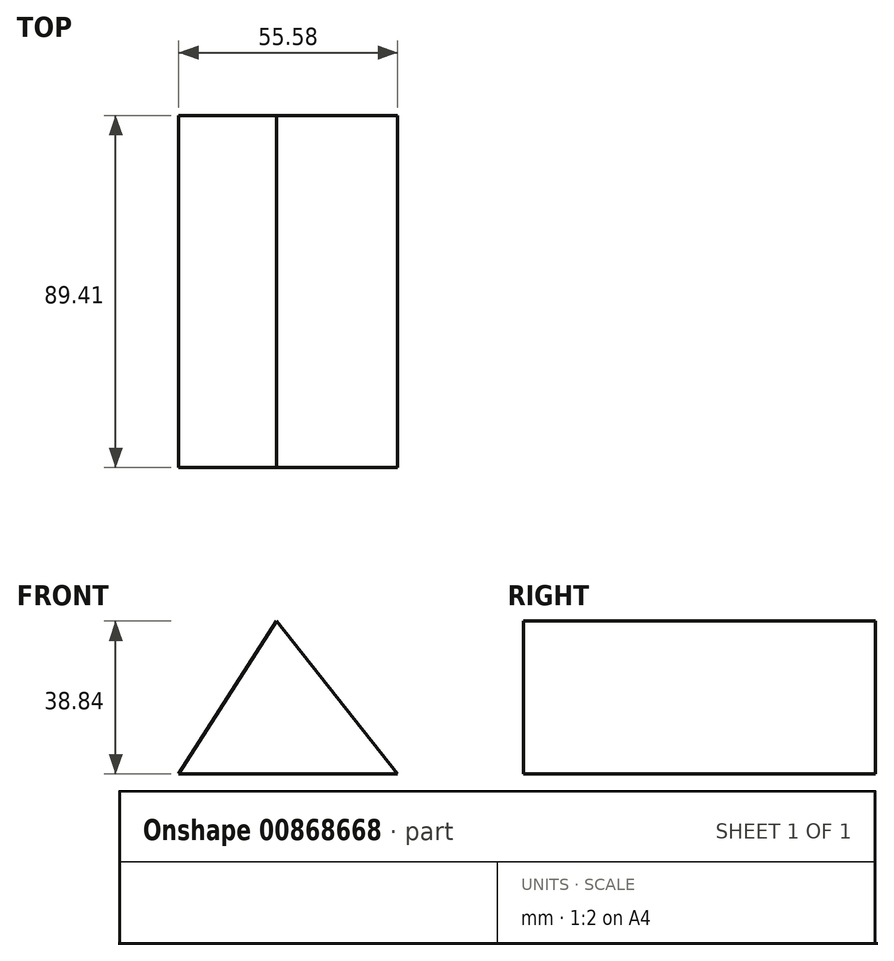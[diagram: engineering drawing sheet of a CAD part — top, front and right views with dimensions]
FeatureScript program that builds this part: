
annotation { "Feature Type Name" : "Feature", "Feature Type Description" : "" }
export const myFeature = defineFeature(function(context is Context, id is Id, definition is map)
    precondition{}
    {
        {
            var Q0;
            Q0=qCreatedBy(makeId("Front.planeOp"),FACE);
            var sketch = newSketch(context, id + "F0", { "sketchPlane" : qUnion([Q0])});
            skLineSegment(sketch, "E0", {"start": v(-11.05, 35.47) * mm, "end": v(-35.93, -3.37) * mm});
            skLineSegment(sketch, "E1", {"start": v(-35.93, -3.37) * mm, "end": v(19.65, -3.37) * mm});
            skLineSegment(sketch, "E2", {"start": v(19.65, -3.37) * mm, "end": v(-11.05, 35.47) * mm});
            skSolve(sketch);
        }
        {
            var Q0;
            Q0=makeQuery(id+"F0.imprint","IMPRINT",FACE,{"disambiguationData":[TD([[makeQuery(id+"F0.imprint","IMPRINT",EDGE,{"derivedFrom":sQuery(id+"F0.wireOp",EDGE,"E0")}),1.0]])]});
            extrude(context, id + "F1", {"entities" : qUnion([Q0]), "depth" : 89.4 * mm, "offsetDistance" : 25.4 * mm});
        }
    });
